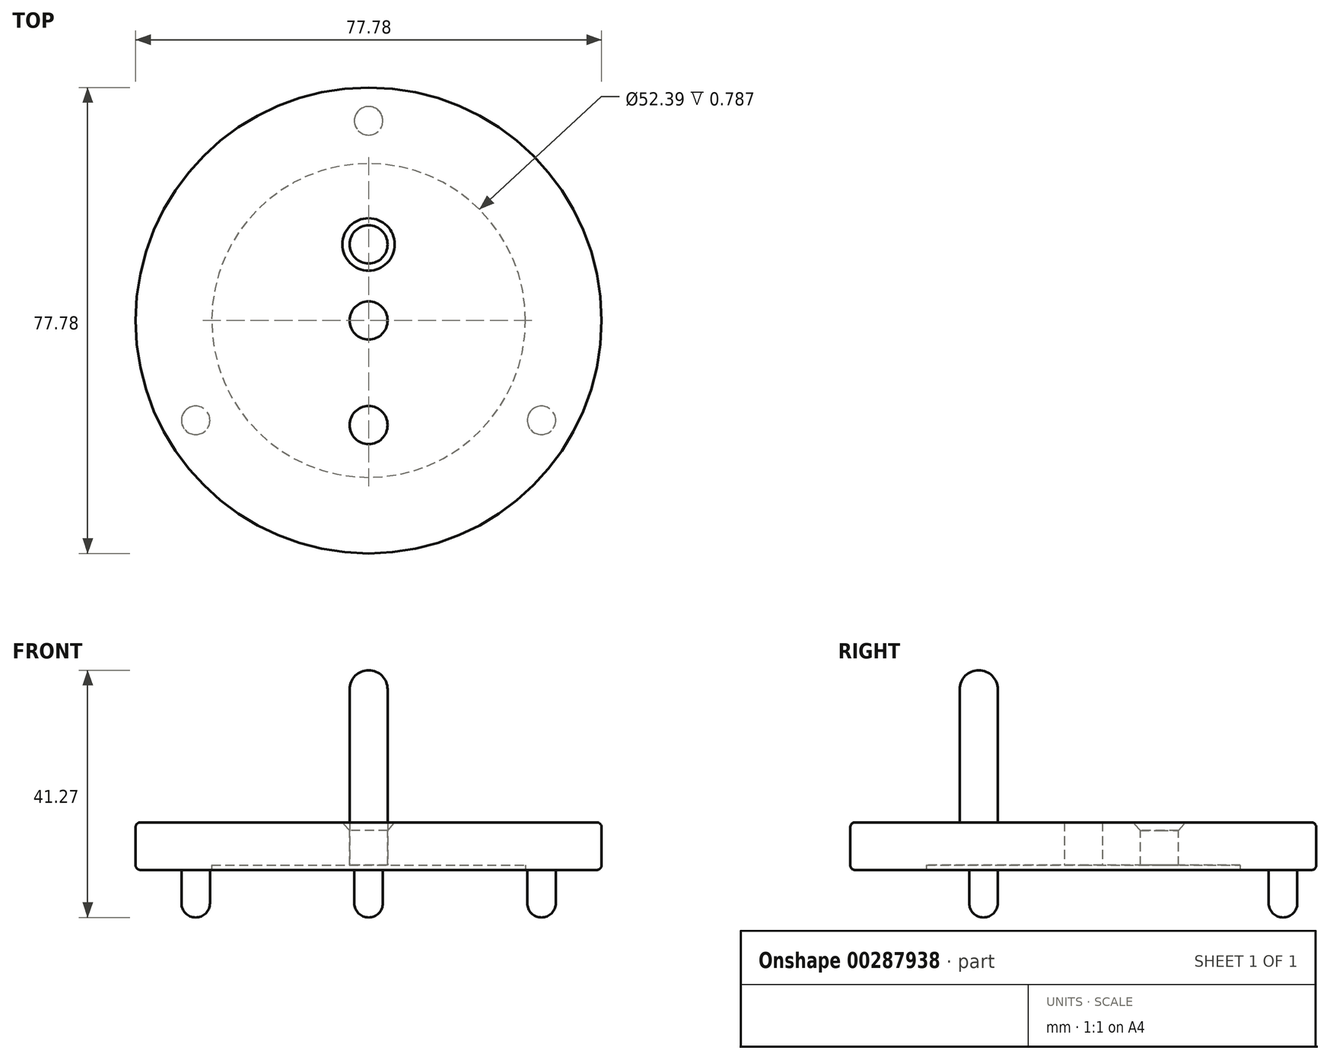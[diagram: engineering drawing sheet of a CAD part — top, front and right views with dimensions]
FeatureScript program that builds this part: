
annotation { "Feature Type Name" : "Feature", "Feature Type Description" : "" }
export const myFeature = defineFeature(function(context is Context, id is Id, definition is map)
    precondition{}
    {
        {
            var Q0;
            Q0=qCreatedBy(makeId("Top.planeOp"),FACE);
            var sketch = newSketch(context, id + "F0", { "sketchPlane" : qUnion([Q0])});
            skCircle(sketch, "E0", {"center": v(0, 0) * mm, "radius": 38.9 * mm});
            skCircle(sketch, "E1", {"center": v(0, 0) * mm, "radius": 3.18 * mm});
            skCircle(sketch, "E2", {"center": v(0, -17.46) * mm, "radius": 3.18 * mm});
            skPoint(sketch, "E3", {"position": v(0, 12.7) * mm});
            skSolve(sketch);
        }
        {
            var Q0;
            Q0=makeQuery(id+"F0.imprint","IMPRINT",FACE,{"disambiguationData":[TD([[makeQuery(id+"F0.imprint","IMPRINT",EDGE,{"derivedFrom":sQuery(id+"F0.wireOp",EDGE,"E0")}),1.0]])]});
            extrude(context, id + "F1", {"entities" : qUnion([Q0]), "depth" : 7.94 * mm, "offsetDistance" : 25.4 * mm});
        }
        {
            var Q0;
            Q0=makeQuery(id+"F0.imprint","IMPRINT",FACE,{"disambiguationData":[TD([[makeQuery(id+"F0.imprint","IMPRINT",EDGE,{"derivedFrom":sQuery(id+"F0.wireOp",EDGE,"E2")}),1.0]])]});
            extrude(context, id + "F2", {"entities" : qUnion([Q0]), "operationType" : NewBodyOperationType.ADD, "depth" : 30.16 * mm, "offsetDistance" : 25.4 * mm});
        }
        {
            var Q0;
            Q0=makeQuery(id+"F2.opExtrude","CAP_FACE",FACE,{"disambiguationData":[OSD([sQuery(id+"F0.wireOp",EDGE,"E2")])],"isStart":false});
            var sketch = newSketch(context, id + "F3", { "sketchPlane" : qUnion([Q0])});
            skLineSegment(sketch, "E4", {"start": v(0, -14.29) * mm, "end": v(0, -20.64) * mm});
            skSolve(sketch);
        }
        {
            var Q0;
            {var subQ0=sQuery(id+"F3.wireOp",EDGE,"E4");Q0=makeQuery(id+"F3.imprint","IMPRINT",FACE,{"disambiguationData":[TD([[makeQuery(id+"F3.imprint","IMPRINT",EDGE,{"derivedFrom":subQ0}),1.0]])]});}
            var Q1;
            Q1=sQuery(id+"F3.wireOp",EDGE,"E4");
            revolve(context, id + "F4", {"operationType" : NewBodyOperationType.ADD, "entities" : qUnion([Q0]), "axis" : qUnion([Q1]), "revolveType" : RevolveType.ONE_DIRECTION, "angle" : 180 * degree});
        }
        {
            var Q0;
            Q0=makeQuery(id+"F1.opExtrude","CAP_FACE",FACE,{"disambiguationData":[OSD([sQuery(id+"F0.wireOp",EDGE,"E0"),sQuery(id+"F0.wireOp",EDGE,"E1"),sQuery(id+"F0.wireOp",EDGE,"E2")])],"isStart":false});
            var sketch = newSketch(context, id + "F5", { "sketchPlane" : qUnion([Q0])});
            skPoint(sketch, "E5", {"position": v(0, 12.7) * mm});
            skSolve(sketch);
        }
        {
            var Q0;
            Q0=sQuery(id+"F5.wireOp",VERTEX,"E5");
            var Q1;
            Q1=makeQuery(id+"F1.opExtrude","SWEPT_BODY",BODY,{"disambiguationData":[OSD([sQuery(id+"F0.wireOp",EDGE,"E0"),sQuery(id+"F0.wireOp",EDGE,"E1"),sQuery(id+"F0.wireOp",EDGE,"E2")])]});
            hole(context, id + "F6", {"style" : HoleStyle.C_SINK, "endStyle" : HoleEndStyle.THROUGH, "holeDiameter" : 6.35 * mm, "cSinkDiameter" : 8.74 * mm, "cSinkAngle" : 82 * degree, "majorDiameter" : 6.35 * mm, "isTappedThrough" : true, "tappedDepth" : 21.59 * mm, "tapClearance" : 3, "locations" : qUnion([Q0]), "scope" : qUnion([Q1])});
        }
        {
            var Q0;
            {var subQ0=sQuery(id+"F0.wireOp",EDGE,"E2");Q0=makeQuery(id+"F2.boolean.opBoolean","MERGE",FACE,{"derivedFrom":[makeQuery(id+"F1.opExtrude","CAP_FACE",FACE,{"disambiguationData":[OSD([sQuery(id+"F0.wireOp",EDGE,"E0"),sQuery(id+"F0.wireOp",EDGE,"E1"),subQ0])],"isStart":true}),makeQuery(id+"F2.opExtrude","CAP_FACE",FACE,{"disambiguationData":[OSD([subQ0])],"isStart":true})]});}
            var sketch = newSketch(context, id + "F7", { "sketchPlane" : qUnion([Q0])});
            skCircle(sketch, "E6", {"center": v(0, 0) * mm, "radius": 26.2 * mm});
            skCircle(sketch, "E7", {"center": v(0, -33.34) * mm, "radius": 2.38 * mm});
            skCircle(sketch, "E8.1.0", {"center": v(28.87, 16.67) * mm, "radius": 2.38 * mm});
            skCircle(sketch, "E8.2.0", {"center": v(-28.87, 16.67) * mm, "radius": 2.38 * mm});
            skSolve(sketch);
        }
        {
            var Q0;
            Q0=makeQuery(id+"F7.imprint","IMPRINT",FACE,{"disambiguationData":[TD([[makeQuery(id+"F7.imprint","IMPRINT",EDGE,{"derivedFrom":sQuery(id+"F7.wireOp",EDGE,"E6")}),1.0]])]});
            extrude(context, id + "F8", {"entities" : qUnion([Q0]), "operationType" : NewBodyOperationType.REMOVE, "oppositeDirection" : true, "depth" : 0.79 * mm, "offsetDistance" : 25.4 * mm});
        }
        {
            var Q0;
            Q0=makeQuery(id+"F7.imprint","IMPRINT",FACE,{"disambiguationData":[TD([[makeQuery(id+"F7.imprint","IMPRINT",EDGE,{"derivedFrom":sQuery(id+"F7.wireOp",EDGE,"E7")}),1.0]])]});
            var Q1;
            Q1=makeQuery(id+"F7.imprint","IMPRINT",FACE,{"disambiguationData":[TD([[makeQuery(id+"F7.imprint","IMPRINT",EDGE,{"derivedFrom":sQuery(id+"F7.wireOp",EDGE,"E8.2.0")}),1.0]])]});
            var Q2;
            Q2=makeQuery(id+"F7.imprint","IMPRINT",FACE,{"disambiguationData":[TD([[makeQuery(id+"F7.imprint","IMPRINT",EDGE,{"derivedFrom":sQuery(id+"F7.wireOp",EDGE,"E8.1.0")}),1.0]])]});
            extrude(context, id + "F9", {"entities" : qUnion([Q0, Q1, Q2]), "operationType" : NewBodyOperationType.ADD, "depth" : 5.55 * mm, "offsetDistance" : 25.4 * mm});
        }
        {
            var Q0;
            Q0=makeQuery(id+"F9.opExtrude","CAP_FACE",FACE,{"disambiguationData":[OSD([sQuery(id+"F7.wireOp",EDGE,"E8.2.0")])],"isStart":false});
            var sketch = newSketch(context, id + "F10", { "sketchPlane" : qUnion([Q0])});
            skLineSegment(sketch, "E9", {"start": v(-28.87, 16.67) * mm, "end": v(-28.87, 19.05) * mm});
            skLineSegment(sketch, "E10", {"start": v(-28.87, 19.05) * mm, "end": v(-28.87, 14.29) * mm});
            skSolve(sketch);
        }
        {
            var Q0;
            Q0=makeQuery(id+"F9.opExtrude","CAP_FACE",FACE,{"disambiguationData":[OSD([sQuery(id+"F7.wireOp",EDGE,"E8.1.0")])],"isStart":false});
            var sketch = newSketch(context, id + "F11", { "sketchPlane" : qUnion([Q0])});
            skLineSegment(sketch, "E11", {"start": v(28.87, 16.67) * mm, "end": v(28.87, 19.05) * mm});
            skLineSegment(sketch, "E12", {"start": v(28.87, 19.05) * mm, "end": v(28.87, 14.29) * mm});
            skSolve(sketch);
        }
        {
            var Q0;
            Q0=makeQuery(id+"F9.opExtrude","CAP_FACE",FACE,{"disambiguationData":[OSD([sQuery(id+"F7.wireOp",EDGE,"E7")])],"isStart":false});
            var sketch = newSketch(context, id + "F12", { "sketchPlane" : qUnion([Q0])});
            skLineSegment(sketch, "E13", {"start": v(0, -33.34) * mm, "end": v(0, -30.96) * mm});
            skLineSegment(sketch, "E14", {"start": v(0, -30.96) * mm, "end": v(0, -35.72) * mm});
            skSolve(sketch);
        }
        {
            var Q0;
            {var subQ0=sQuery(id+"F12.wireOp",EDGE,"E14");var subQ3=makeQuery(id+"F12.imprint","IMPRINT",VERTEX,{"derivedFrom":subQ0});Q0=makeQuery(id+"F12.imprint","IMPRINT",FACE,{"disambiguationData":[TD([[makeQuery(id+"F12.imprint","IMPRINT",EDGE,{"disambiguationData":[TD([[subQ3,1.0]])],"derivedFrom":subQ0}),1.0]])]});}
            var Q1;
            Q1=sQuery(id+"F12.wireOp",EDGE,"E14");
            revolve(context, id + "F13", {"operationType" : NewBodyOperationType.ADD, "entities" : qUnion([Q0]), "axis" : qUnion([Q1]), "revolveType" : RevolveType.ONE_DIRECTION, "angle" : 180 * degree});
        }
        {
            var Q0;
            {var subQ0=sQuery(id+"F11.wireOp",EDGE,"E12");var subQ3=makeQuery(id+"F11.imprint","IMPRINT",VERTEX,{"derivedFrom":subQ0});Q0=makeQuery(id+"F11.imprint","IMPRINT",FACE,{"disambiguationData":[TD([[makeQuery(id+"F11.imprint","IMPRINT",EDGE,{"disambiguationData":[TD([[subQ3,1.0]])],"derivedFrom":subQ0}),1.0]])]});}
            var Q1;
            Q1=sQuery(id+"F11.wireOp",EDGE,"E12");
            revolve(context, id + "F14", {"operationType" : NewBodyOperationType.ADD, "entities" : qUnion([Q0]), "axis" : qUnion([Q1]), "revolveType" : RevolveType.ONE_DIRECTION, "angle" : 180 * degree});
        }
        {
            var Q0;
            {var subQ0=sQuery(id+"F10.wireOp",EDGE,"E10");var subQ3=makeQuery(id+"F10.imprint","IMPRINT",VERTEX,{"derivedFrom":subQ0});Q0=makeQuery(id+"F10.imprint","IMPRINT",FACE,{"disambiguationData":[TD([[makeQuery(id+"F10.imprint","IMPRINT",EDGE,{"disambiguationData":[TD([[subQ3,1.0]])],"derivedFrom":subQ0}),1.0]])]});}
            var Q1;
            Q1=sQuery(id+"F10.wireOp",EDGE,"E10");
            revolve(context, id + "F15", {"operationType" : NewBodyOperationType.ADD, "entities" : qUnion([Q0]), "axis" : qUnion([Q1]), "revolveType" : RevolveType.ONE_DIRECTION, "angle" : 180 * degree});
        }
        {
            var Q0;
            Q0=makeQuery(id+"F1.opExtrude","CAP_EDGE",EDGE,{"disambiguationData":[OSD([sQuery(id+"F0.wireOp",EDGE,"E0")])],"isStart":false});
            var Q1;
            Q1=makeQuery(id+"F1.opExtrude","CAP_EDGE",EDGE,{"disambiguationData":[OSD([sQuery(id+"F0.wireOp",EDGE,"E0")])],"isStart":true});
            fillet(context, id + "F16", {"entities" : qUnion([Q0, Q1]), "radius" : 0.79 * mm, "tangentPropagation" : true, "allowEdgeOverflow" : false});
        }
    });
